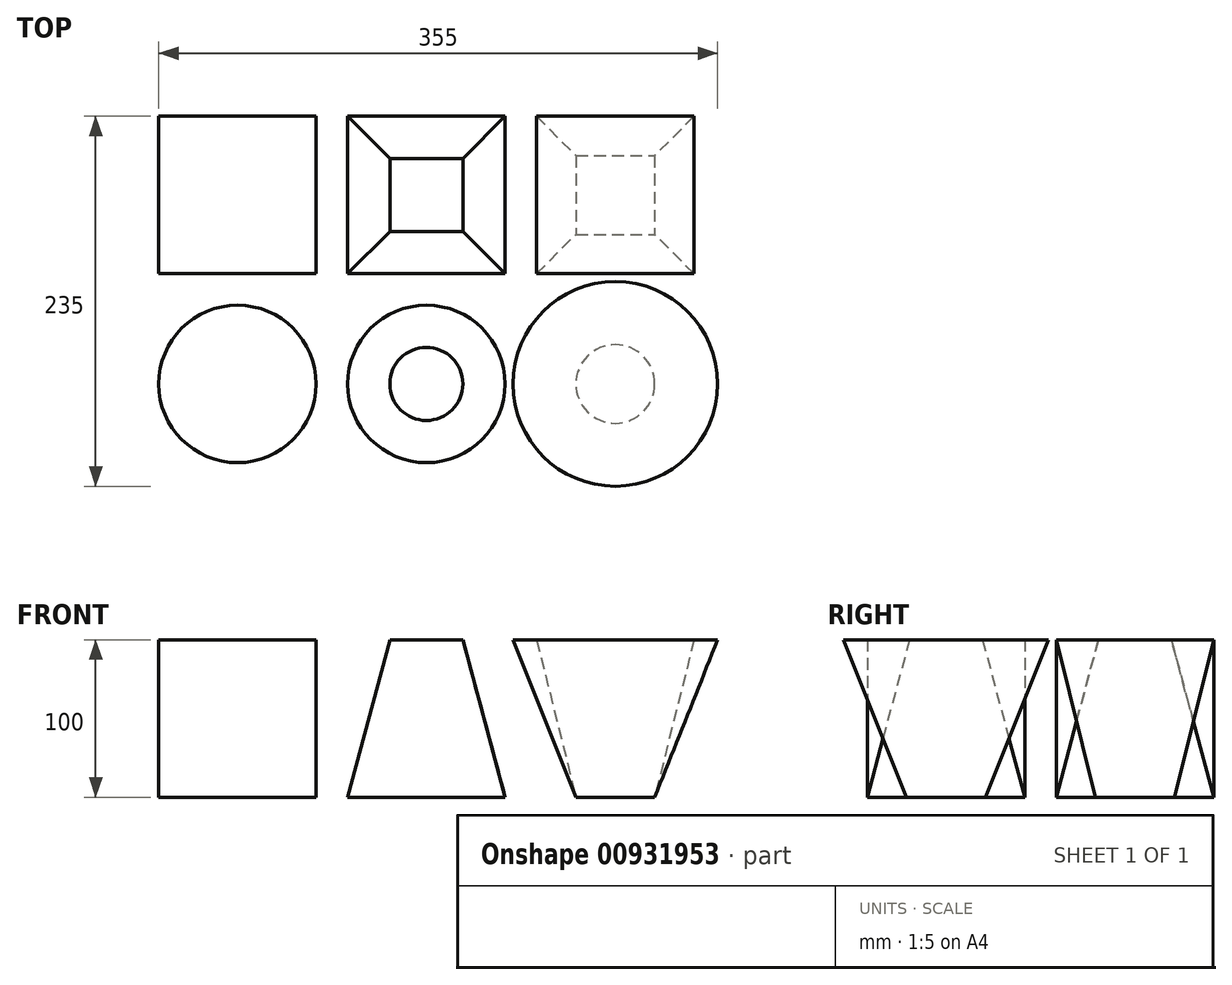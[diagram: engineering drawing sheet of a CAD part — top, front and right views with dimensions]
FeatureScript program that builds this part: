
annotation { "Feature Type Name" : "Feature", "Feature Type Description" : "" }
export const myFeature = defineFeature(function(context is Context, id is Id, definition is map)
    precondition{}
    {
        {
            var Q0;
            Q0=qCreatedBy(makeId("Top.planeOp"),FACE);
            var sketch = newSketch(context, id + "F0", { "sketchPlane" : qUnion([Q0])});
            skCircle(sketch, "E0", {"center": v(0, 0) * mm, "radius": 50 * mm});
            skLineSegment(sketch, "E1", {"start": v(0, 0) * mm, "end": v(120, 0) * mm, "construction": true});
            skCircle(sketch, "E2", {"center": v(120, 0) * mm, "radius": 50 * mm});
            skLineSegment(sketch, "E3", {"start": v(120, 0) * mm, "end": v(240, 0) * mm, "construction": true});
            skCircle(sketch, "E4", {"center": v(240, 0) * mm, "radius": 50 * mm});
            skLineSegment(sketch, "E5", {"start": v(240, 0) * mm, "end": v(240, 120) * mm, "construction": true});
            skLineSegment(sketch, "E6", {"start": v(240, 120) * mm, "end": v(120, 120) * mm, "construction": true});
            skLineSegment(sketch, "E7", {"start": v(120, 120) * mm, "end": v(0, 120) * mm, "construction": true});
            skLineSegment(sketch, "E8", {"start": v(0, 0) * mm, "end": v(0, 120) * mm, "construction": true});
            skLineSegment(sketch, "E9.bottom", {"start": v(-50, 170) * mm, "end": v(50, 170) * mm});
            skLineSegment(sketch, "E9.top", {"start": v(-50, 70) * mm, "end": v(50, 70) * mm});
            skLineSegment(sketch, "E9.left", {"start": v(-50, 170) * mm, "end": v(-50, 70) * mm});
            skLineSegment(sketch, "E9.right", {"start": v(50, 170) * mm, "end": v(50, 70) * mm});
            skLineSegment(sketch, "E10.bottom", {"start": v(70, 170) * mm, "end": v(170, 170) * mm});
            skLineSegment(sketch, "E10.top", {"start": v(70, 70) * mm, "end": v(170, 70) * mm});
            skLineSegment(sketch, "E10.left", {"start": v(70, 170) * mm, "end": v(70, 70) * mm});
            skLineSegment(sketch, "E10.right", {"start": v(170, 170) * mm, "end": v(170, 70) * mm});
            skLineSegment(sketch, "E11.bottom", {"start": v(190, 170) * mm, "end": v(290, 170) * mm});
            skLineSegment(sketch, "E11.top", {"start": v(190, 70) * mm, "end": v(290, 70) * mm});
            skLineSegment(sketch, "E11.left", {"start": v(190, 170) * mm, "end": v(190, 70) * mm});
            skLineSegment(sketch, "E11.right", {"start": v(290, 170) * mm, "end": v(290, 70) * mm});
            skLineSegment(sketch, "E12", {"start": v(-50, 120) * mm, "end": v(290, 120) * mm, "construction": true});
            skPoint(sketch, "E13", {"position": v(290, 120) * mm});
            skPoint(sketch, "E14", {"position": v(70, 120) * mm});
            skLineSegment(sketch, "E15", {"start": v(50, 170) * mm, "end": v(-50, 70) * mm, "construction": true});
            skLineSegment(sketch, "E16", {"start": v(170, 170) * mm, "end": v(70, 70) * mm, "construction": true});
            skLineSegment(sketch, "E17", {"start": v(290, 170) * mm, "end": v(190, 70) * mm, "construction": true});
            skCircle(sketch, "E18", {"center": v(240, 0) * mm, "radius": 25 * mm});
            skLineSegment(sketch, "E19.bottom", {"start": v(215, 145) * mm, "end": v(265, 145) * mm});
            skLineSegment(sketch, "E19.top", {"start": v(215, 95) * mm, "end": v(265, 95) * mm});
            skLineSegment(sketch, "E19.left", {"start": v(215, 145) * mm, "end": v(215, 95) * mm});
            skLineSegment(sketch, "E19.right", {"start": v(265, 145) * mm, "end": v(265, 95) * mm});
            skLineSegment(sketch, "E20", {"start": v(265, 95) * mm, "end": v(265, 0) * mm, "construction": true});
            skSolve(sketch);
        }
        {
            var Q0;
            Q0=makeQuery(id+"F0.imprint","IMPRINT",FACE,{"disambiguationData":[TD([[makeQuery(id+"F0.imprint","IMPRINT",EDGE,{"derivedFrom":sQuery(id+"F0.wireOp",EDGE,"E0")}),1.0]])]});
            var Q1;
            Q1=sQuery(id+"F0.wireOp",EDGE,"E0");
            extrude(context, id + "F1", {"entities" : qUnion([Q0]), "surfaceEntities" : qUnion([Q1]), "depth" : 100 * mm, "offsetDistance" : 25 * mm});
        }
        {
            var Q0;
            Q0=makeQuery(id+"F1.opExtrude","CAP_FACE",FACE,{"disambiguationData":[OSD([sQuery(id+"F0.wireOp",EDGE,"E0")])],"isStart":false});
            cPlane(context, id + "F2", {"entities" : qUnion([Q0]), "cplaneType" : CPlaneType.OFFSET, "offset" : 0 * mm, "width" : 150 * mm, "height" : 150 * mm});
        }
        {
            var Q0;
            Q0=makeQuery(id+"F0.imprint","IMPRINT",FACE,{"disambiguationData":[TD([[makeQuery(id+"F0.imprint","IMPRINT",EDGE,{"derivedFrom":sQuery(id+"F0.wireOp",EDGE,"E2")}),1.0]])]});
            var Q1;
            Q1=sQuery(id+"F0.wireOp",EDGE,"E2");
            extrude(context, id + "F3", {"entities" : qUnion([Q0]), "surfaceEntities" : qUnion([Q1]), "depth" : 100 * mm, "offsetDistance" : 25 * mm, "hasDraft" : true, "draftAngle" : 15 * degree, "draftPullDirection" : true});
        }
        {
            var Q0;
            Q0=qCreatedBy(id+"F2.planeOp",FACE);
            var sketch = newSketch(context, id + "F4", { "sketchPlane" : qUnion([Q0])});
            skCircle(sketch, "E21", {"center": v(240, 0) * mm, "radius": 65 * mm});
            skSolve(sketch);
        }
        {
            var Q0;
            Q0=makeQuery(id+"F4.imprint","IMPRINT",FACE,{"disambiguationData":[TD([[makeQuery(id+"F4.imprint","IMPRINT",EDGE,{"derivedFrom":sQuery(id+"F4.wireOp",EDGE,"E21")}),1.0]])]});
            var Q1;
            Q1=makeQuery(id+"F0.imprint","IMPRINT",FACE,{"disambiguationData":[TD([[makeQuery(id+"F0.imprint","IMPRINT",EDGE,{"derivedFrom":sQuery(id+"F0.wireOp",EDGE,"E18")}),1.0]])]});
            loft(context, id + "F5", {"sheetProfilesArray" : [{ "sheetProfileEntities" : qUnion([Q0]) }, { "sheetProfileEntities" : qUnion([Q1]) }]});
        }
        {
            var Q0;
            Q0=makeQuery(id+"F0.imprint","IMPRINT",FACE,{"disambiguationData":[TD([[makeQuery(id+"F0.imprint","IMPRINT",EDGE,{"derivedFrom":sQuery(id+"F0.wireOp",EDGE,"E10.bottom")}),-1.0]])]});
            extrude(context, id + "F6", {"entities" : qUnion([Q0]), "depth" : 100 * mm, "offsetDistance" : 25 * mm, "hasDraft" : true, "draftAngle" : 15 * degree, "draftPullDirection" : true});
        }
        {
            var Q0;
            Q0=makeQuery(id+"F0.imprint","IMPRINT",FACE,{"disambiguationData":[TD([[makeQuery(id+"F0.imprint","IMPRINT",EDGE,{"derivedFrom":sQuery(id+"F0.wireOp",EDGE,"E9.bottom")}),-1.0]])]});
            extrude(context, id + "F7", {"entities" : qUnion([Q0]), "depth" : 100 * mm, "offsetDistance" : 25 * mm});
        }
        {
            var Q0;
            Q0=qCreatedBy(id+"F2.planeOp",FACE);
            var sketch = newSketch(context, id + "F8", { "sketchPlane" : qUnion([Q0])});
            skLineSegment(sketch, "E22.0.0", {"start": v(190, 170) * mm, "end": v(190, 70) * mm});
            skLineSegment(sketch, "E22.0.1", {"start": v(190, 70) * mm, "end": v(290, 70) * mm});
            skLineSegment(sketch, "E22.0.2", {"start": v(290, 70) * mm, "end": v(290, 170) * mm});
            skLineSegment(sketch, "E22.0.3", {"start": v(290, 170) * mm, "end": v(190, 170) * mm});
            skSolve(sketch);
        }
        {
            var Q0;
            Q0=makeQuery(id+"F8.imprint","IMPRINT",FACE,{"disambiguationData":[TD([[makeQuery(id+"F8.imprint","IMPRINT",EDGE,{"derivedFrom":sQuery(id+"F8.wireOp",EDGE,"E22.0.0")}),1.0]])]});
            var Q1;
            Q1=makeQuery(id+"F0.imprint","IMPRINT",FACE,{"disambiguationData":[TD([[makeQuery(id+"F0.imprint","IMPRINT",EDGE,{"derivedFrom":sQuery(id+"F0.wireOp",EDGE,"E19.bottom")}),-1.0]])]});
            loft(context, id + "F9", {"sheetProfilesArray" : [{ "sheetProfileEntities" : qUnion([Q0]) }, { "sheetProfileEntities" : qUnion([Q1]) }]});
        }
    });
